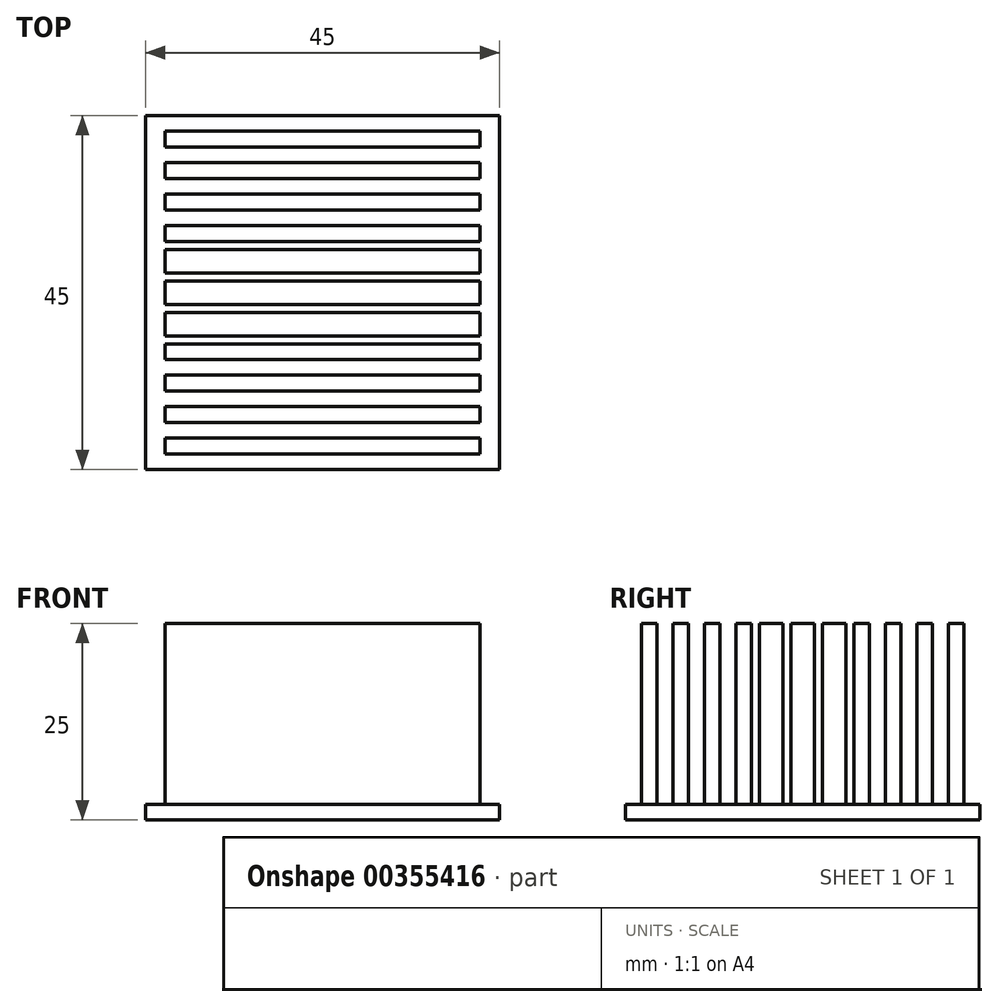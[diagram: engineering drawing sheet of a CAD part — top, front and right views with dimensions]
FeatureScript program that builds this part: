
annotation { "Feature Type Name" : "Feature", "Feature Type Description" : "" }
export const myFeature = defineFeature(function(context is Context, id is Id, definition is map)
    precondition{}
    {
        {
            var Q0;
            Q0=qCreatedBy(makeId("Top.planeOp"),FACE);
            var sketch = newSketch(context, id + "F0", { "sketchPlane" : qUnion([Q0])});
            skLineSegment(sketch, "E0.bottom", {"start": v(-22.5, 22.5) * mm, "end": v(22.5, 22.5) * mm});
            skLineSegment(sketch, "E0.top", {"start": v(-22.5, -22.5) * mm, "end": v(22.5, -22.5) * mm});
            skLineSegment(sketch, "E0.left", {"start": v(-22.5, 22.5) * mm, "end": v(-22.5, -22.5) * mm});
            skLineSegment(sketch, "E0.right", {"start": v(22.5, 22.5) * mm, "end": v(22.5, -22.5) * mm});
            skSolve(sketch);
        }
        {
            var Q0;
            Q0 = qSketchRegion(id + "F0", true);
            extrude(context, id + "F1", {"entities" : qUnion([Q0]), "depth" : 25 * mm});
        }
        {
            var Q0;
            Q0=makeQuery(id+"F1.opExtrude","CAP_FACE",FACE,{"disambiguationData":[OSD([sQuery(id+"F0.wireOp",EDGE,"E0.bottom"),sQuery(id+"F0.wireOp",EDGE,"E0.top"),sQuery(id+"F0.wireOp",EDGE,"E0.left"),sQuery(id+"F0.wireOp",EDGE,"E0.right")])],"isStart":false});
            var sketch = newSketch(context, id + "F2", { "sketchPlane" : qUnion([Q0])});
            skLineSegment(sketch, "E1", {"start": v(-22.5, 22.5) * mm, "end": v(22.5, 22.5) * mm});
            skLineSegment(sketch, "E2", {"start": v(22.5, 22.5) * mm, "end": v(22.5, -22.5) * mm});
            skLineSegment(sketch, "E3", {"start": v(22.5, -22.5) * mm, "end": v(-22.5, -22.5) * mm});
            skLineSegment(sketch, "E4", {"start": v(-22.5, -22.5) * mm, "end": v(-22.5, 22.5) * mm});
            skLineSegment(sketch, "E5.bottom", {"start": v(-20, 20.5) * mm, "end": v(20, 20.5) * mm});
            skLineSegment(sketch, "E5.top", {"start": v(-20, 18.5) * mm, "end": v(20, 18.5) * mm});
            skLineSegment(sketch, "E5.left", {"start": v(-20, 20.5) * mm, "end": v(-20, 18.5) * mm});
            skLineSegment(sketch, "E5.right", {"start": v(20, 20.5) * mm, "end": v(20, 18.5) * mm});
            skLineSegment(sketch, "E6.bottom", {"start": v(-20, 16.5) * mm, "end": v(20, 16.5) * mm});
            skLineSegment(sketch, "E6.top", {"start": v(-20, 14.5) * mm, "end": v(20, 14.5) * mm});
            skLineSegment(sketch, "E6.left", {"start": v(-20, 16.5) * mm, "end": v(-20, 14.5) * mm});
            skLineSegment(sketch, "E6.right", {"start": v(20, 16.5) * mm, "end": v(20, 14.5) * mm});
            skLineSegment(sketch, "E7.bottom", {"start": v(-20, 12.5) * mm, "end": v(20, 12.5) * mm});
            skLineSegment(sketch, "E7.top", {"start": v(-20, 10.5) * mm, "end": v(20, 10.5) * mm});
            skLineSegment(sketch, "E7.left", {"start": v(-20, 12.5) * mm, "end": v(-20, 10.5) * mm});
            skLineSegment(sketch, "E7.right", {"start": v(20, 12.5) * mm, "end": v(20, 10.5) * mm});
            skLineSegment(sketch, "E8.bottom", {"start": v(-20, 8.5) * mm, "end": v(20, 8.5) * mm});
            skLineSegment(sketch, "E8.top", {"start": v(-20, 6.5) * mm, "end": v(20, 6.5) * mm});
            skLineSegment(sketch, "E8.left", {"start": v(-20, 8.5) * mm, "end": v(-20, 6.5) * mm});
            skLineSegment(sketch, "E8.right", {"start": v(20, 8.5) * mm, "end": v(20, 6.5) * mm});
            skLineSegment(sketch, "E9.bottom", {"start": v(-20, 4.5) * mm, "end": v(20, 4.5) * mm});
            skLineSegment(sketch, "E9.top", {"start": v(-20, 2.5) * mm, "end": v(20, 2.5) * mm});
            skLineSegment(sketch, "E9.left", {"start": v(-20, 4.5) * mm, "end": v(-20, 2.5) * mm});
            skLineSegment(sketch, "E9.right", {"start": v(20, 4.5) * mm, "end": v(20, 2.5) * mm});
            skLineSegment(sketch, "E10.bottom", {"start": v(-20, 0.5) * mm, "end": v(20, 0.5) * mm});
            skLineSegment(sketch, "E10.top", {"start": v(-20, -1.5) * mm, "end": v(20, -1.5) * mm});
            skLineSegment(sketch, "E10.left", {"start": v(-20, 0.5) * mm, "end": v(-20, -1.5) * mm});
            skLineSegment(sketch, "E10.right", {"start": v(20, 0.5) * mm, "end": v(20, -1.5) * mm});
            skLineSegment(sketch, "E11.bottom", {"start": v(-20, -3.5) * mm, "end": v(20, -3.5) * mm});
            skLineSegment(sketch, "E11.top", {"start": v(-20, -5.5) * mm, "end": v(20, -5.5) * mm});
            skLineSegment(sketch, "E11.left", {"start": v(-20, -3.5) * mm, "end": v(-20, -5.5) * mm});
            skLineSegment(sketch, "E11.right", {"start": v(20, -3.5) * mm, "end": v(20, -5.5) * mm});
            skLineSegment(sketch, "E12.MirrorCS", {"start": v(-20, -12.5) * mm, "end": v(-20, -10.5) * mm});
            skLineSegment(sketch, "E13.MirrorCS", {"start": v(20, -12.5) * mm, "end": v(20, -10.5) * mm});
            skLineSegment(sketch, "E14.MirrorCS", {"start": v(20, -0.5) * mm, "end": v(20, 1.5) * mm});
            skLineSegment(sketch, "E15.MirrorCS", {"start": v(20, -4.5) * mm, "end": v(20, -2.5) * mm});
            skLineSegment(sketch, "E16.MirrorCS", {"start": v(-20, -20.5) * mm, "end": v(-20, -18.5) * mm});
            skLineSegment(sketch, "E17.MirrorCS", {"start": v(20, -20.5) * mm, "end": v(20, -18.5) * mm});
            skLineSegment(sketch, "E18.MirrorCS", {"start": v(-20, -16.5) * mm, "end": v(-20, -14.5) * mm});
            skLineSegment(sketch, "E19.MirrorCS", {"start": v(20, -16.5) * mm, "end": v(20, -14.5) * mm});
            skLineSegment(sketch, "E20.MirrorCS", {"start": v(20, -8.5) * mm, "end": v(20, -6.5) * mm});
            skLineSegment(sketch, "E21.MirrorCS", {"start": v(-20, -0.5) * mm, "end": v(-20, 1.5) * mm});
            skLineSegment(sketch, "E22.MirrorCS", {"start": v(-20, -4.5) * mm, "end": v(-20, -2.5) * mm});
            skLineSegment(sketch, "E23.MirrorCS", {"start": v(20, 3.5) * mm, "end": v(20, 5.5) * mm});
            skLineSegment(sketch, "E24.MirrorCS", {"start": v(-20, 3.5) * mm, "end": v(-20, 5.5) * mm});
            skLineSegment(sketch, "E25.MirrorCS", {"start": v(-20, -8.5) * mm, "end": v(-20, -6.5) * mm});
            skLineSegment(sketch, "E26.MirrorCS", {"start": v(-20, -10.5) * mm, "end": v(20, -10.5) * mm});
            skLineSegment(sketch, "E27.MirrorCS", {"start": v(-20, -20.5) * mm, "end": v(20, -20.5) * mm});
            skLineSegment(sketch, "E28.MirrorCS", {"start": v(-20, -6.5) * mm, "end": v(20, -6.5) * mm});
            skLineSegment(sketch, "E29.MirrorCS", {"start": v(-20, -18.5) * mm, "end": v(20, -18.5) * mm});
            skLineSegment(sketch, "E30.MirrorCS", {"start": v(-20, 5.5) * mm, "end": v(20, 5.5) * mm});
            skLineSegment(sketch, "E31.MirrorCS", {"start": v(-20, -4.5) * mm, "end": v(20, -4.5) * mm});
            skLineSegment(sketch, "E32.MirrorCS", {"start": v(-20, -16.5) * mm, "end": v(20, -16.5) * mm});
            skLineSegment(sketch, "E33.MirrorCS", {"start": v(-20, -14.5) * mm, "end": v(20, -14.5) * mm});
            skLineSegment(sketch, "E34.MirrorCS", {"start": v(-20, -8.5) * mm, "end": v(20, -8.5) * mm});
            skLineSegment(sketch, "E35.MirrorCS", {"start": v(-20, 3.5) * mm, "end": v(20, 3.5) * mm});
            skLineSegment(sketch, "E36.MirrorCS", {"start": v(-20, -0.5) * mm, "end": v(20, -0.5) * mm});
            skLineSegment(sketch, "E37.MirrorCS", {"start": v(-20, -12.5) * mm, "end": v(20, -12.5) * mm});
            skLineSegment(sketch, "E38.MirrorCS", {"start": v(-20, 1.5) * mm, "end": v(20, 1.5) * mm});
            skLineSegment(sketch, "E39.MirrorCS", {"start": v(-20, -2.5) * mm, "end": v(20, -2.5) * mm});
            skSolve(sketch);
        }
        {
            var Q0;
            Q0 = qSketchRegion(id + "F2", true);
            extrude(context, id + "F3", {"entities" : qUnion([Q0]), "operationType" : NewBodyOperationType.REMOVE, "oppositeDirection" : true, "depth" : 23 * mm});
        }
    });
